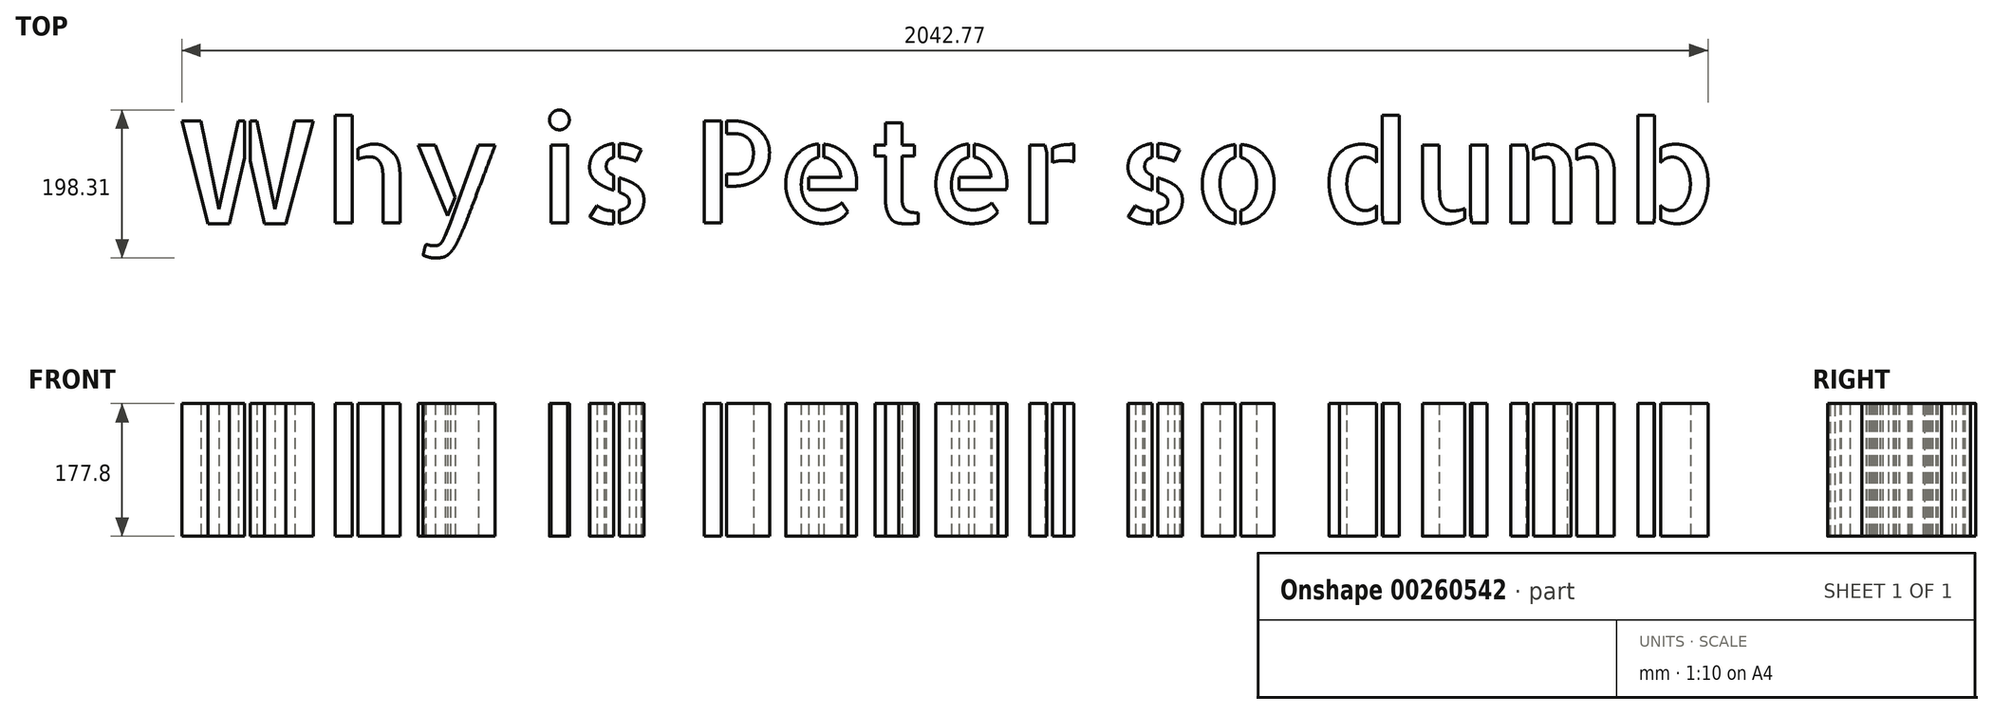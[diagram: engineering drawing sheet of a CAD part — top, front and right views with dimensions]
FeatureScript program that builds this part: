
annotation { "Feature Type Name" : "Feature", "Feature Type Description" : "" }
export const myFeature = defineFeature(function(context is Context, id is Id, definition is map)
    precondition{}
    {
        {
            var Q0;
            Q0=qCreatedBy(makeId("Top.planeOp"),FACE);
            var sketch = newSketch(context, id + "F0", { "sketchPlane" : qUnion([Q0])});
            skText(sketch, "E0", { "text": "Why is Peter so dumb", "fontName": "AllertaStencil-Regular.ttf"});
            const initialGuessF0  = {"E0": [-0.07533, -0.07504, 1, 0, 0.1369]};
            skSetInitialGuess(sketch, initialGuessF0);
            skSolve(sketch);
        }
        {
            var Q0;
            Q0 = qSketchRegion(id + "F0", true);
            extrude(context, id + "F1", {"entities" : qUnion([Q0]), "depth" : 177.8 * mm});
        }
    });
